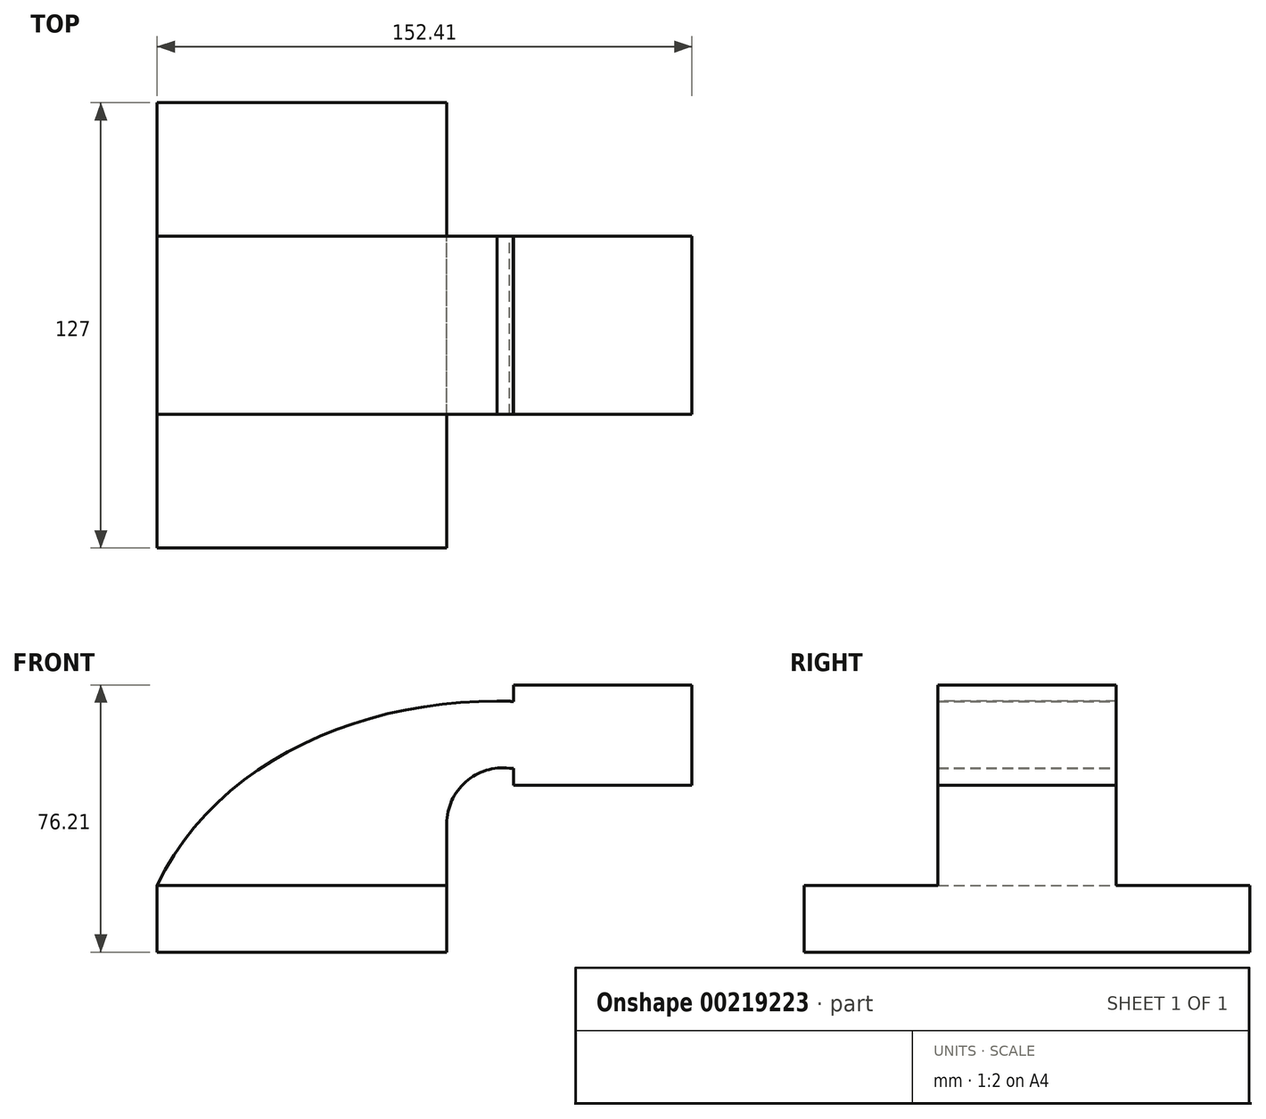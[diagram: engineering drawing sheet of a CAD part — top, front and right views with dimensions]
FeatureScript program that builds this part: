
annotation { "Feature Type Name" : "Feature", "Feature Type Description" : "" }
export const myFeature = defineFeature(function(context is Context, id is Id, definition is map)
    precondition{}
    {
        {
            var Q0;
            Q0=qCreatedBy(makeId("Front.planeOp"),FACE);
            var sketch = newSketch(context, id + "F0", { "sketchPlane" : qUnion([Q0])});
            skLineSegment(sketch, "E0.bottom", {"start": v(41.27, 9.53) * mm, "end": v(-41.28, 9.53) * mm});
            skLineSegment(sketch, "E0.top", {"start": v(41.28, -9.52) * mm, "end": v(-41.27, -9.52) * mm});
            skLineSegment(sketch, "E0.left", {"start": v(41.28, 9.53) * mm, "end": v(41.28, -9.52) * mm});
            skLineSegment(sketch, "E0.right", {"start": v(-41.28, 9.53) * mm, "end": v(-41.27, -9.52) * mm});
            skPoint(sketch, "E0.middle", {"position": v(0, 0) * mm});
            skLineSegment(sketch, "E1.bottom", {"start": v(60.33, 66.68) * mm, "end": v(111.13, 66.68) * mm});
            skLineSegment(sketch, "E1.top", {"start": v(60.33, 38.1) * mm, "end": v(111.13, 38.1) * mm});
            skLineSegment(sketch, "E1.left", {"start": v(60.33, 66.68) * mm, "end": v(60.33, 38.1) * mm});
            skLineSegment(sketch, "E1.right", {"start": v(111.13, 66.68) * mm, "end": v(111.13, 38.1) * mm});
            skPoint(sketch, "E1.middle", {"position": v(85.73, 52.39) * mm});
            skLineSegment(sketch, "E2", {"start": v(41.27, 9.53) * mm, "end": v(41.27, 27.13) * mm});
            skArc(sketch, "E3", {"start": v(41.27, 27.13) * mm, "mid": v(46.66, 39.04) * mm, "end": v(59.15, 42.88) * mm});
            skLineSegment(sketch, "E4", {"start": v(59.15, 42.88) * mm, "end": v(85.73, 42.88) * mm});
            skLineSegment(sketch, "E5.0", {"start": v(60.12, 61.93) * mm, "end": v(85.73, 61.93) * mm});
            skArc(sketch, "E5.1", {"start": v(22.23, 27.13) * mm, "mid": v(33.53, 52.85) * mm, "end": v(60.12, 61.93) * mm});
            skLineSegment(sketch, "E5.2", {"start": v(22.22, 9.53) * mm, "end": v(22.22, 27.13) * mm});
            skLineSegment(sketch, "E6", {"start": v(85.73, 38.1) * mm, "end": v(85.73, 66.68) * mm});
            skFitSpline(sketch, "E7", {"points": [v(-41.28, 9.53) * mm, v(60.12, 61.93) * mm], "startDerivative": vector(50.52, 107.36) * mm, "endDerivative": vector(125.13, -4.73) * mm});
            skSolve(sketch);
        }
        {
            var Q0;
            Q0=makeQuery(id+"F0.imprint","IMPRINT",FACE,{"disambiguationData":[TD([[makeQuery(id+"F0.imprint","IMPRINT",EDGE,{"derivedFrom":sQuery(id+"F0.wireOp",EDGE,"E0.top")}),-1.0]])]});
            extrude(context, id + "F1", {"entities" : qUnion([Q0]), "endBound" : BoundingType.SYMMETRIC, "depth" : 127 * mm});
        }
        {
            var Q0;
            Q0 = qSketchRegion(id + "F0", true);
            extrude(context, id + "F2", {"entities" : qUnion([Q0]), "operationType" : NewBodyOperationType.ADD, "endBound" : BoundingType.SYMMETRIC, "depth" : 50.8 * mm});
        }
    });
